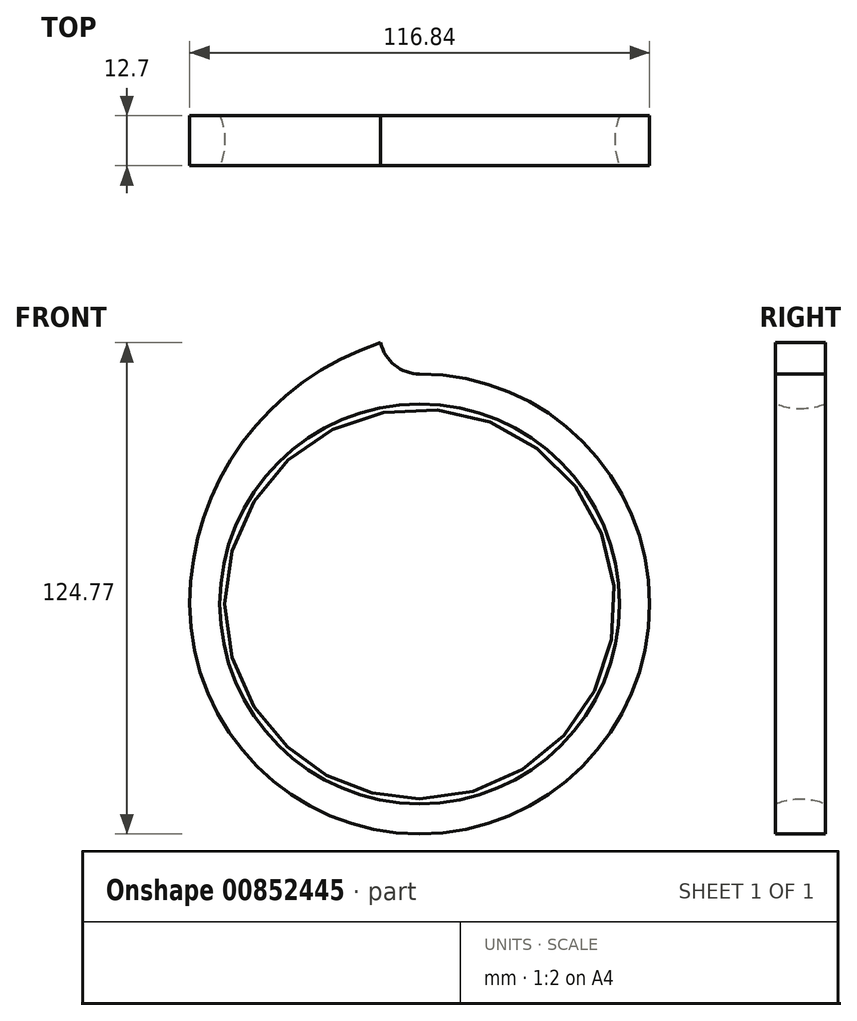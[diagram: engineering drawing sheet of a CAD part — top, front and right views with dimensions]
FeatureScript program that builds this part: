
annotation { "Feature Type Name" : "Feature", "Feature Type Description" : "" }
export const myFeature = defineFeature(function(context is Context, id is Id, definition is map)
    precondition{}
    {
        {
            var Q0;
            Q0=qCreatedBy(makeId("Front.planeOp"),FACE);
            var sketch = newSketch(context, id + "F0", { "sketchPlane" : qUnion([Q0])});
            skCircle(sketch, "E0", {"center": v(0, 0) * mm, "radius": 50.8 * mm});
            skCircle(sketch, "E1", {"center": v(0, 0) * mm, "radius": 58.42 * mm});
            skArc(sketch, "E2", {"start": v(-9.91, 66.35) * mm, "mid": v(-45, 41.1) * mm, "end": v(-58.42, 0) * mm});
            skArc(sketch, "E3", {"start": v(-9.91, 66.35) * mm, "mid": v(-6.35, 60.65) * mm, "end": v(0, 58.42) * mm});
            skLineSegment(sketch, "E4", {"start": v(-9.91, 66.35) * mm, "end": v(-11.24, 72.28) * mm, "construction": true});
            skLineSegment(sketch, "E5", {"start": v(-9.91, 66.35) * mm, "end": v(-1.12, 69.15) * mm, "construction": true});
            skSolve(sketch);
        }
        {
            var Q0;
            Q0=makeQuery(id+"F0.imprint","IMPRINT",FACE,{"disambiguationData":[TD([[makeQuery(id+"F0.imprint","IMPRINT",EDGE,{"derivedFrom":sQuery(id+"F0.wireOp",EDGE,"E0")}),-1.0]])]});
            var Q1;
            {var subQ0=sQuery(id+"F0.wireOp",EDGE,"E2");Q1=makeQuery(id+"F0.imprint","IMPRINT",FACE,{"disambiguationData":[TD([[makeQuery(id+"F0.imprint","IMPRINT",EDGE,{"derivedFrom":subQ0}),1.0]])]});}
            extrude(context, id + "F1", {"entities" : qUnion([Q0, Q1]), "endBound" : BoundingType.SYMMETRIC, "depth" : 12.7 * mm, "offsetDistance" : 25.4 * mm});
        }
        {
            var Q0;
            Q0=qCreatedBy(makeId("Right.planeOp"),FACE);
            var sketch = newSketch(context, id + "F2", { "sketchPlane" : qUnion([Q0])});
            skLineSegment(sketch, "E6", {"start": v(-6.35, 50.8) * mm, "end": v(6.35, 50.8) * mm});
            skArc(sketch, "E7", {"start": v(-6.35, 50.8) * mm, "mid": v(0, 49.53) * mm, "end": v(6.35, 50.8) * mm});
            skPoint(sketch, "E8", {"position": v(0, 50.8) * mm});
            skLineSegment(sketch, "E9", {"start": v(-55.24, 0) * mm, "end": v(58.73, 0) * mm, "construction": true});
            skSolve(sketch);
        }
        {
            var Q0;
            Q0=makeQuery(id+"F2.imprint","IMPRINT",FACE,{"disambiguationData":[TD([[makeQuery(id+"F2.imprint","IMPRINT",EDGE,{"derivedFrom":sQuery(id+"F2.wireOp",EDGE,"E6")}),-1.0]])]});
            var Q1;
            Q1=sQuery(id+"F2.wireOp",EDGE,"E9");
            revolve(context, id + "F3", {"operationType" : NewBodyOperationType.ADD, "surfaceOperationType" : NewSurfaceOperationType.NEW, "entities" : qUnion([Q0]), "axis" : qUnion([Q1]), "revolveType" : RevolveType.FULL});
        }
    });
